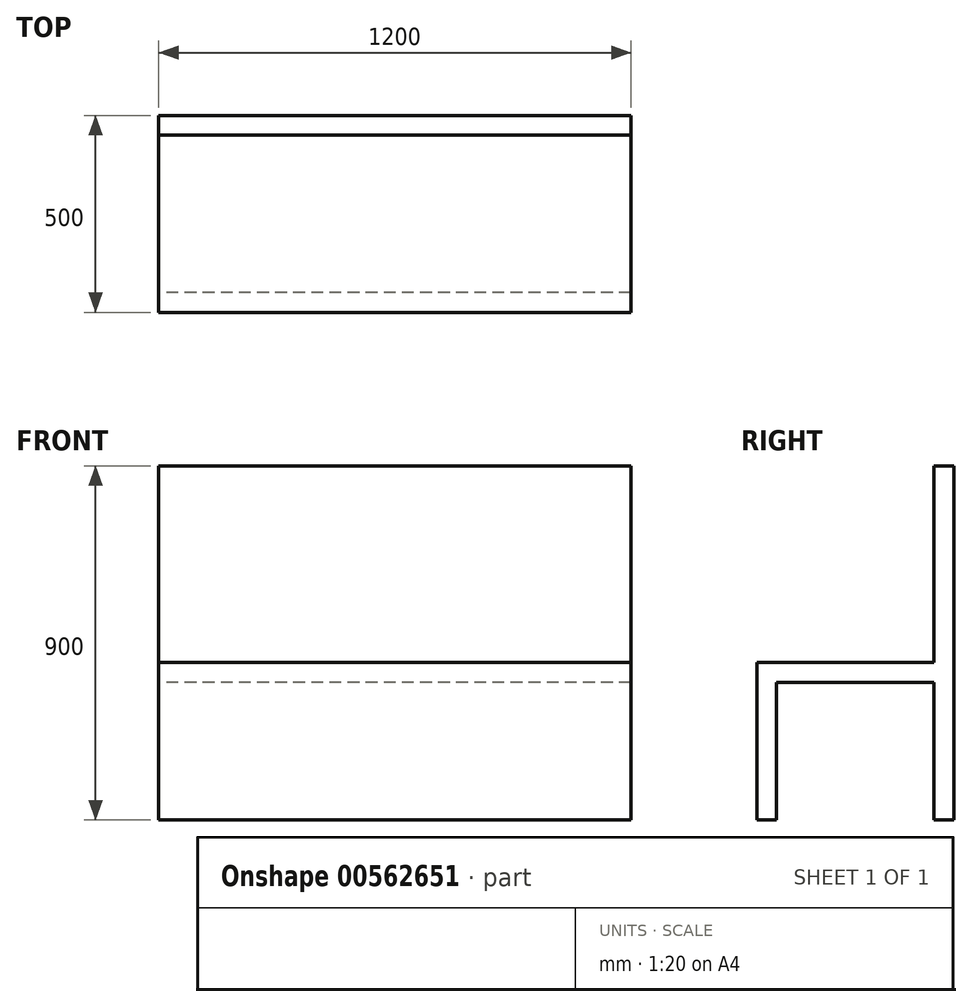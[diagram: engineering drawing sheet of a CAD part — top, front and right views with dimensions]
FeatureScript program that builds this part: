
annotation { "Feature Type Name" : "Feature", "Feature Type Description" : "" }
export const myFeature = defineFeature(function(context is Context, id is Id, definition is map)
    precondition{}
    {
        {
            var Q0;
            Q0=qCreatedBy(makeId("Right.planeOp"),FACE);
            var sketch = newSketch(context, id + "F0", { "sketchPlane" : qUnion([Q0])});
            skLineSegment(sketch, "E0.bottom", {"start": v(-500, 0) * mm, "end": v(-450, 0) * mm});
            skLineSegment(sketch, "E0.left", {"start": v(-500, 0) * mm, "end": v(-500, 400) * mm});
            skLineSegment(sketch, "E0.right", {"start": v(0, 0) * mm, "end": v(0, 900) * mm});
            skLineSegment(sketch, "E1.top", {"start": v(-50, 900) * mm, "end": v(0, 900) * mm});
            skLineSegment(sketch, "E1.left", {"start": v(-50, 400) * mm, "end": v(-50, 900) * mm});
            skLineSegment(sketch, "E2.top", {"start": v(-450, 350) * mm, "end": v(-50, 350) * mm});
            skLineSegment(sketch, "E2.left", {"start": v(-450, 0) * mm, "end": v(-450, 350) * mm});
            skLineSegment(sketch, "E2.right", {"start": v(-50, 0) * mm, "end": v(-50, 350) * mm});
            skLineSegment(sketch, "E3.trimOffspring", {"start": v(-50, 0) * mm, "end": v(0, 0) * mm});
            skLineSegment(sketch, "E4", {"start": v(-500, 400) * mm, "end": v(-50, 400) * mm});
            skSolve(sketch);
        }
        {
            var Q0;
            Q0 = qSketchRegion(id + "F0", true);
            extrude(context, id + "F1", {"entities" : qUnion([Q0]), "depth" : 1200 * mm, "offsetDistance" : 25 * mm, "symmetric" : true});
        }
        {
            var Q0;
            Q0=qCreatedBy(makeId("Front.planeOp"),FACE);
            cPlane(context, id + "F2", {"entities" : qUnion([Q0]), "cplaneType" : CPlaneType.OFFSET, "offset" : 500 * mm, "width" : 150 * mm, "height" : 150 * mm});
        }
    });
